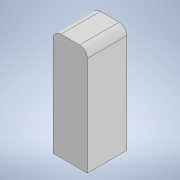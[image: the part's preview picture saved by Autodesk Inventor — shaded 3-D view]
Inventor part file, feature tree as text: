
AUTODESK INVENTOR PART (.ipt)
format: ipt  version: 2020 (Build 240168000, 168)  size: 96,256 bytes
history: native  units: in
note: dims shown in document units (in); Inventor stores cm internally (conversion verified against a paired STEP export)
features: extrude x1, fillet x1, sketch x1
ambient origin geometry x8: Origin, YZ Plane, XZ Plane, XY Plane, X Axis, Y Axis, Z Axis, Center Point
bodies: Solid1 (feature_tree)
feature tree (3):
  extrude  "Extrusion1"  Depth=2.1995in
  fillet  "Fillet1"  Radius=6.875in
  sketch  "Sketch1"  dims[d0=2.535in d1=2.1995in d2=6.875in d3=0.0in d4=0.5in]
